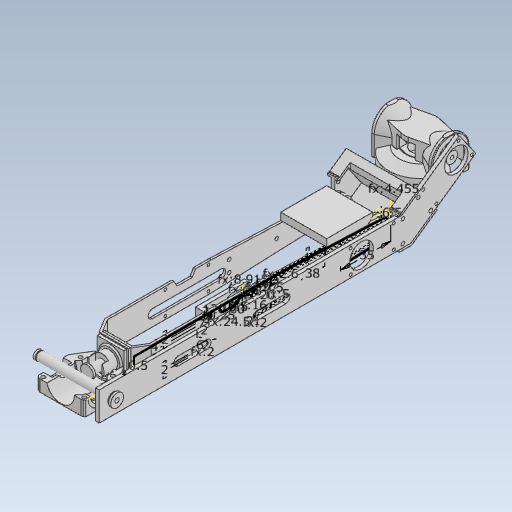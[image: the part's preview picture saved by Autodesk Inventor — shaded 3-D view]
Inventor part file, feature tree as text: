
AUTODESK INVENTOR PART (.ipt)
format: ipt  version: 2024 (Build 280153000, 153)  size: 1,749,504 bytes
history: native  units: mm
features: other x40, extrude x25, revolve x12, shell x1, mirror x1
ambient origin geometry x8: Origin, YZ Plane, XZ Plane, XY Plane, X Axis, Y Axis, Z Axis, Center Point
bodies: Body1 (feature_tree), Body2 (feature_tree), Body3 (feature_tree), Body4 (feature_tree), Body5 (feature_tree), Body6 (feature_tree), Body7 (feature_tree), Body8 (feature_tree), Body9 (feature_tree), Body10 (feature_tree), Body11 (feature_tree), Body12 (feature_tree), Body13 (feature_tree), Body14 (feature_tree), Body15 (feature_tree)
feature tree (79):
  other  "front_shoulderGear"
  other  "front_shoulderUnit"
  other  "front_shoulderUnit-cover"
  other  "作業平面7"
  other  "top_shoulderUnit-largeGearShaft_smallGearShaft"
  other  "作業平面5"
  other  "top_shoulderUnit-largeGearShaft_baseWasher"
  other  "作業平面4"
  other  "side_links-link1_link1Conn"
  other  "作業平面6"
  other  "vtop_links-link1_link1Conn"
  other  "作業平面9"
  other  "作業平面10"
  other  "top_elbowGear"
  other  "top_elbowUnit"
  other  "front_elbowUnit_links-link2shaft"
  other  "作業平面11"
  other  "作業平面12"
  other  "top_links-link2_wristUnit"
  other  "side_links-link2"
  other  "作業平面13"
  other  "作業平面14"
  other  "top_wristUnit"
  other  "side_wristUnit"
  revolve  "回転1"
  revolve  "回転2"
  extrude  "押し出し5"  Depth=40.59mm
  extrude  "押し出し11"  Depth=7.07mm
  extrude  "押し出し13"  Depth=1.6mm
  extrude  "押し出し12"  Depth=6.78mm
  revolve  "回転3"
  extrude  "押し出し18"  Depth=22.41mm
  revolve  "回転4"
  extrude  "押し出し20"  Depth=21.0mm
  extrude  "押し出し9"  Depth=14.0mm
  revolve  "回転6"
  other  "厚み1"
  extrude  "押し出し19"  Depth=40.0mm
  revolve  "回転7"
  shell  "シェル2"  Thickness=20.0mm
  extrude  "押し出し21"  Depth=40.59mm
  mirror  "ミラー6"
  extrude  "elb"  Depth=22.41mm
  revolve  "回転11"
  revolve  "回転12"
  extrude  "押し出し17"  Depth=1.6mm
  revolve  "回転14"
  extrude  "押し出し39"  Depth=6.78mm
  extrude  "押し出し27"  Depth=21.0mm
  extrude  "押し出し30"  Depth=4.636476mm
  extrude  "押し出し32"  Depth=26.58mm
  extrude  "押し出し29"  Depth=4.0mm
  extrude  "押し出し25"  Depth=26.58mm
  extrude  "押し出し33"  Depth=26.0mm
  revolve  "回転20"
  extrude  "押し出し26"  Depth=15.0mm
  extrude  "押し出し31"  Depth=5.0mm
  revolve  "回転21"
  revolve  "回転22"
  other  "wrist"
  extrude  "押し出し36"  Depth=9.17mm
  extrude  "押し出し37"  Depth=5.0mm
  extrude  "押し出し38"  Depth=2.0mm
  extrude  "押し出し40"  TaperAngle=360.0deg  [1 undecoded]
  extrude  "押し出し41"  Depth=5.0mm
  other  "ソリッド6"
  other  "ソリッド8"
  other  "ソリッド9"
  other  "ソリッド13"
  other  "ソリッド15"
  other  "ソリッド16"
  other  "ソリッド18"
  other  "ソリッド24"
  other  "ソリッド27"
  other  "ソリッド28"
  other  "ソリッド29"
  other  "ソリッド31"
  other  "ソリッド32"
  other  "ソリッド33"
note: 1 required parameter value undecoded (feature->parameter linkage not recoverable at this tier; creation-order binding heuristic only, values carry confidence <= 0.55)
